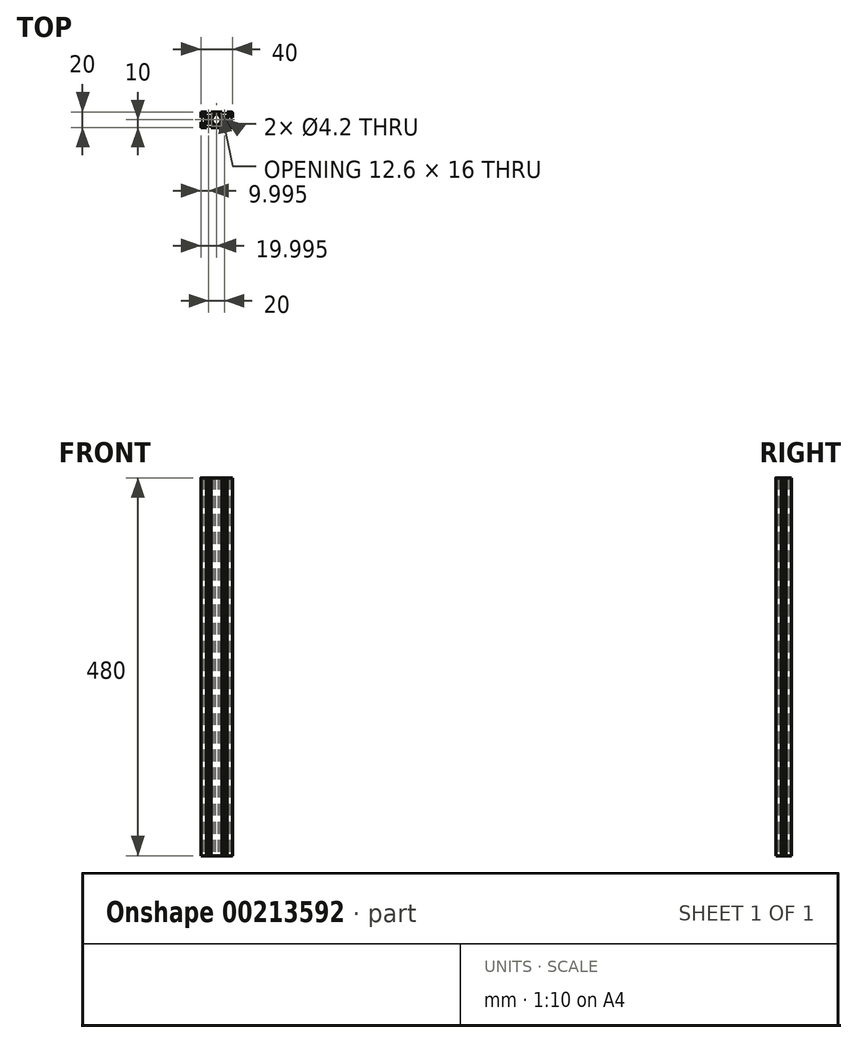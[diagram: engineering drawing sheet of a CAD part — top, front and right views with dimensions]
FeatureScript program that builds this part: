
annotation { "Feature Type Name" : "Feature", "Feature Type Description" : "" }
export const myFeature = defineFeature(function(context is Context, id is Id, definition is map)
    precondition{}
    {
        {
            var Q0;
            Q0=qCreatedBy(makeId("Top.planeOp"),FACE);
            var sketch = newSketch(context, id + "F0", { "sketchPlane" : qUnion([Q0])});
            skLineSegment(sketch, "E0.MirrorCS", {"start": v(6.14, -0.52) * mm, "end": v(6.44, 0) * mm});
            skLineSegment(sketch, "E1.MirrorCS", {"start": v(13.84, 0) * mm, "end": v(14.14, -0.52) * mm});
            skLineSegment(sketch, "E2.MirrorCS", {"start": v(10.65, -4) * mm, "end": v(10.14, -3.7) * mm});
            skLineSegment(sketch, "E3.MirrorCS", {"start": v(10.14, -3.7) * mm, "end": v(9.62, -4) * mm});
            skLineSegment(sketch, "E4.MirrorCS", {"start": v(4.14, -8) * mm, "end": v(7.14, -8) * mm});
            skLineSegment(sketch, "E5.MirrorCS", {"start": v(6.14, -2.94) * mm, "end": v(6.14, -0.52) * mm});
            skLineSegment(sketch, "E6.MirrorCS", {"start": v(16.14, -7.06) * mm, "end": v(13.07, -4) * mm});
            skLineSegment(sketch, "E7.MirrorCS", {"start": v(7.14, -8) * mm, "end": v(7.14, -10) * mm});
            skLineSegment(sketch, "E8.MirrorCS", {"start": v(20.14, -3) * mm, "end": v(20.14, -9) * mm});
            skLineSegment(sketch, "E9.MirrorCS", {"start": v(9.62, -4) * mm, "end": v(7.2, -4) * mm});
            skArc(sketch, "E10.MirrorCS", {"start": v(20.14, -9) * mm, "mid": v(19.84, -9.7) * mm, "end": v(19.14, -10) * mm});
            skLineSegment(sketch, "E11.MirrorCS", {"start": v(19.14, -10) * mm, "end": v(13.14, -10) * mm});
            skLineSegment(sketch, "E12.MirrorCS", {"start": v(13.07, -4) * mm, "end": v(10.65, -4) * mm});
            skLineSegment(sketch, "E13.MirrorCS", {"start": v(13.14, -10) * mm, "end": v(13.14, -8) * mm});
            skLineSegment(sketch, "E14.MirrorCS", {"start": v(14.14, -0.52) * mm, "end": v(14.14, -2.94) * mm});
            skLineSegment(sketch, "E15.MirrorCS", {"start": v(14.14, -2.94) * mm, "end": v(17.2, -6) * mm});
            skLineSegment(sketch, "E16.MirrorCS", {"start": v(17.2, -6) * mm, "end": v(18.14, -6) * mm});
            skLineSegment(sketch, "E17.MirrorCS", {"start": v(18.14, -6) * mm, "end": v(18.14, -3) * mm});
            skLineSegment(sketch, "E18.MirrorCS", {"start": v(18.14, -3) * mm, "end": v(20.14, -3) * mm});
            skLineSegment(sketch, "E19.MirrorCS", {"start": v(7.2, -4) * mm, "end": v(4.14, -7.06) * mm});
            skLineSegment(sketch, "E20.MirrorCS", {"start": v(13.14, -8) * mm, "end": v(16.14, -8) * mm});
            skLineSegment(sketch, "E21.MirrorCS", {"start": v(4.14, -7.06) * mm, "end": v(4.14, -8) * mm});
            skLineSegment(sketch, "E22.MirrorCS", {"start": v(16.14, -8) * mm, "end": v(16.14, -7.06) * mm});
            skLineSegment(sketch, "E23.MirrorCS", {"start": v(3.07, -6) * mm, "end": v(6.14, -2.94) * mm});
            skCircle(sketch, "E24", {"center": v(10.14, 0) * mm, "radius": 2.1 * mm});
            skLineSegment(sketch, "E25", {"start": v(3.07, -6) * mm, "end": v(2.01, -7.06) * mm});
            skLineSegment(sketch, "E26", {"start": v(2.01, -7.06) * mm, "end": v(2.01, -8) * mm});
            skLineSegment(sketch, "E27.MirrorCS", {"start": v(-10.38, -4) * mm, "end": v(-9.86, -3.7) * mm});
            skLineSegment(sketch, "E28.MirrorCS", {"start": v(-9.86, -3.7) * mm, "end": v(-9.35, -4) * mm});
            skLineSegment(sketch, "E29.MirrorCS", {"start": v(-13.56, 0) * mm, "end": v(-13.86, -0.52) * mm});
            skLineSegment(sketch, "E30.MirrorCS", {"start": v(-5.86, -0.52) * mm, "end": v(-6.16, 0) * mm});
            skLineSegment(sketch, "E31.MirrorCS", {"start": v(-12.86, -8) * mm, "end": v(-15.86, -8) * mm});
            skLineSegment(sketch, "E32.MirrorCS", {"start": v(-6.86, -8) * mm, "end": v(-6.86, -10) * mm});
            skLineSegment(sketch, "E33.MirrorCS", {"start": v(-19.86, -3) * mm, "end": v(-19.86, -9) * mm});
            skArc(sketch, "E34.MirrorCS", {"start": v(-19.86, -9) * mm, "mid": v(-19.57, -9.7) * mm, "end": v(-18.86, -10) * mm});
            skLineSegment(sketch, "E35.MirrorCS", {"start": v(-9.35, -4) * mm, "end": v(-6.93, -4) * mm});
            skLineSegment(sketch, "E36.MirrorCS", {"start": v(-18.86, -10) * mm, "end": v(-12.86, -10) * mm});
            skCircle(sketch, "E37.MirrorC", {"center": v(-9.86, 0) * mm, "radius": 2.1 * mm});
            skLineSegment(sketch, "E38.MirrorCS", {"start": v(-12.8, -4) * mm, "end": v(-10.38, -4) * mm});
            skLineSegment(sketch, "E39.MirrorCS", {"start": v(-17.86, -6) * mm, "end": v(-17.86, -3) * mm});
            skLineSegment(sketch, "E40.MirrorCS", {"start": v(-15.86, -8) * mm, "end": v(-15.86, -7.06) * mm});
            skLineSegment(sketch, "E41.MirrorCS", {"start": v(-13.86, -0.52) * mm, "end": v(-13.86, -2.94) * mm});
            skLineSegment(sketch, "E42.MirrorCS", {"start": v(-17.86, -3) * mm, "end": v(-19.86, -3) * mm});
            skLineSegment(sketch, "E43.MirrorCS", {"start": v(-13.86, -2.94) * mm, "end": v(-16.93, -6) * mm});
            skLineSegment(sketch, "E44.MirrorCS", {"start": v(-3.86, -8) * mm, "end": v(-6.86, -8) * mm});
            skLineSegment(sketch, "E45.MirrorCS", {"start": v(-15.86, -7.06) * mm, "end": v(-12.8, -4) * mm});
            skLineSegment(sketch, "E46.MirrorCS", {"start": v(-5.86, -2.94) * mm, "end": v(-5.86, -0.52) * mm});
            skLineSegment(sketch, "E47.MirrorCS", {"start": v(-6.93, -4) * mm, "end": v(-3.86, -7.06) * mm});
            skLineSegment(sketch, "E48.MirrorCS", {"start": v(-16.93, -6) * mm, "end": v(-17.86, -6) * mm});
            skLineSegment(sketch, "E49.MirrorCS", {"start": v(-1.74, -7.06) * mm, "end": v(-1.74, -8) * mm});
            skLineSegment(sketch, "E50.MirrorCS", {"start": v(-3.86, -7.06) * mm, "end": v(-3.86, -8) * mm});
            skLineSegment(sketch, "E51.MirrorCS", {"start": v(-2.8, -6) * mm, "end": v(-1.74, -7.06) * mm});
            skLineSegment(sketch, "E52.MirrorCS", {"start": v(-2.8, -6) * mm, "end": v(-5.86, -2.94) * mm});
            skLineSegment(sketch, "E53.MirrorCS", {"start": v(-12.86, -10) * mm, "end": v(-12.86, -8) * mm});
            skLineSegment(sketch, "E54.MirrorCS", {"start": v(10.14, 3.7) * mm, "end": v(9.62, 4) * mm});
            skLineSegment(sketch, "E55.MirrorCS", {"start": v(-10.38, 4) * mm, "end": v(-9.86, 3.7) * mm});
            skLineSegment(sketch, "E56.MirrorCS", {"start": v(10.65, 4) * mm, "end": v(10.14, 3.7) * mm});
            skLineSegment(sketch, "E57.MirrorCS", {"start": v(-9.86, 3.7) * mm, "end": v(-9.35, 4) * mm});
            skLineSegment(sketch, "E58.MirrorCS", {"start": v(13.84, 0) * mm, "end": v(14.14, 0.52) * mm});
            skLineSegment(sketch, "E59.MirrorCS", {"start": v(6.14, 0.52) * mm, "end": v(6.44, 0) * mm});
            skLineSegment(sketch, "E60.MirrorCS", {"start": v(-5.86, 0.52) * mm, "end": v(-6.16, 0) * mm});
            skLineSegment(sketch, "E61.MirrorCS", {"start": v(-13.56, 0) * mm, "end": v(-13.86, 0.52) * mm});
            skLineSegment(sketch, "E62.MirrorCS", {"start": v(-18.86, 10) * mm, "end": v(-12.86, 10) * mm});
            skLineSegment(sketch, "E63.MirrorCS", {"start": v(16.14, 7.06) * mm, "end": v(13.07, 4) * mm});
            skLineSegment(sketch, "E64.MirrorCS", {"start": v(6.14, 2.94) * mm, "end": v(6.14, 0.52) * mm});
            skLineSegment(sketch, "E65.MirrorCS", {"start": v(-3.86, 8) * mm, "end": v(-6.86, 8) * mm});
            skLineSegment(sketch, "E66.MirrorCS", {"start": v(4.14, 8) * mm, "end": v(7.14, 8) * mm});
            skLineSegment(sketch, "E67.MirrorCS", {"start": v(-15.86, 8) * mm, "end": v(-15.86, 7.06) * mm});
            skLineSegment(sketch, "E68.MirrorCS", {"start": v(-3.86, 7.06) * mm, "end": v(-3.86, 8) * mm});
            skArc(sketch, "E69.MirrorCS", {"start": v(20.14, 9) * mm, "mid": v(19.84, 9.7) * mm, "end": v(19.14, 10) * mm});
            skLineSegment(sketch, "E70.MirrorCS", {"start": v(14.14, 2.94) * mm, "end": v(17.2, 6) * mm});
            skLineSegment(sketch, "E71.MirrorCS", {"start": v(3.07, 6) * mm, "end": v(6.14, 2.94) * mm});
            skLineSegment(sketch, "E72.MirrorCS", {"start": v(-9.35, 4) * mm, "end": v(-6.93, 4) * mm});
            skLineSegment(sketch, "E73.MirrorCS", {"start": v(14.14, 0.52) * mm, "end": v(14.14, 2.94) * mm});
            skLineSegment(sketch, "E74.MirrorCS", {"start": v(-2.8, 6) * mm, "end": v(-5.86, 2.94) * mm});
            skLineSegment(sketch, "E75.MirrorCS", {"start": v(-17.86, 6) * mm, "end": v(-17.86, 3) * mm});
            skLineSegment(sketch, "E76.MirrorCS", {"start": v(16.14, 8) * mm, "end": v(16.14, 7.06) * mm});
            skLineSegment(sketch, "E77.MirrorCS", {"start": v(-15.86, 7.06) * mm, "end": v(-12.8, 4) * mm});
            skLineSegment(sketch, "E78.MirrorCS", {"start": v(18.14, 3) * mm, "end": v(20.14, 3) * mm});
            skLineSegment(sketch, "E79.MirrorCS", {"start": v(19.14, 10) * mm, "end": v(13.14, 10) * mm});
            skLineSegment(sketch, "E80.MirrorCS", {"start": v(4.14, 7.06) * mm, "end": v(4.14, 8) * mm});
            skLineSegment(sketch, "E81.MirrorCS", {"start": v(-12.86, 8) * mm, "end": v(-15.86, 8) * mm});
            skLineSegment(sketch, "E82.MirrorCS", {"start": v(-5.86, 2.94) * mm, "end": v(-5.86, 0.52) * mm});
            skLineSegment(sketch, "E83.MirrorCS", {"start": v(13.07, 4) * mm, "end": v(10.65, 4) * mm});
            skLineSegment(sketch, "E84.MirrorCS", {"start": v(-13.86, 2.94) * mm, "end": v(-16.93, 6) * mm});
            skLineSegment(sketch, "E85.MirrorCS", {"start": v(13.14, 8) * mm, "end": v(16.14, 8) * mm});
            skLineSegment(sketch, "E86.MirrorCS", {"start": v(-13.86, 0.52) * mm, "end": v(-13.86, 2.94) * mm});
            skLineSegment(sketch, "E87.MirrorCS", {"start": v(-6.86, 8) * mm, "end": v(-6.86, 10) * mm});
            skLineSegment(sketch, "E88.MirrorCS", {"start": v(20.14, 3) * mm, "end": v(20.14, 9) * mm});
            skLineSegment(sketch, "E89.MirrorCS", {"start": v(-12.8, 4) * mm, "end": v(-10.38, 4) * mm});
            skLineSegment(sketch, "E90.MirrorCS", {"start": v(-12.86, 10) * mm, "end": v(-12.86, 8) * mm});
            skLineSegment(sketch, "E91.MirrorCS", {"start": v(-6.93, 4) * mm, "end": v(-3.86, 7.06) * mm});
            skLineSegment(sketch, "E92.MirrorCS", {"start": v(9.62, 4) * mm, "end": v(7.2, 4) * mm});
            skLineSegment(sketch, "E93.MirrorCS", {"start": v(13.14, 10) * mm, "end": v(13.14, 8) * mm});
            skLineSegment(sketch, "E94.MirrorCS", {"start": v(-16.93, 6) * mm, "end": v(-17.86, 6) * mm});
            skLineSegment(sketch, "E95.MirrorCS", {"start": v(-19.86, 3) * mm, "end": v(-19.86, 9) * mm});
            skLineSegment(sketch, "E96.MirrorCS", {"start": v(3.07, 6) * mm, "end": v(2.01, 7.06) * mm});
            skLineSegment(sketch, "E97.MirrorCS", {"start": v(-17.86, 3) * mm, "end": v(-19.86, 3) * mm});
            skLineSegment(sketch, "E98.MirrorCS", {"start": v(-1.74, 7.06) * mm, "end": v(-1.74, 8) * mm});
            skLineSegment(sketch, "E99.MirrorCS", {"start": v(2.01, 7.06) * mm, "end": v(2.01, 8) * mm});
            skLineSegment(sketch, "E100.MirrorCS", {"start": v(18.14, 6) * mm, "end": v(18.14, 3) * mm});
            skArc(sketch, "E101.MirrorCS", {"start": v(-19.86, 9) * mm, "mid": v(-19.57, 9.7) * mm, "end": v(-18.86, 10) * mm});
            skLineSegment(sketch, "E102.MirrorCS", {"start": v(-2.8, 6) * mm, "end": v(-1.74, 7.06) * mm});
            skLineSegment(sketch, "E103.MirrorCS", {"start": v(7.14, 8) * mm, "end": v(7.14, 10) * mm});
            skLineSegment(sketch, "E104.MirrorCS", {"start": v(17.2, 6) * mm, "end": v(18.14, 6) * mm});
            skLineSegment(sketch, "E105.MirrorCS", {"start": v(7.2, 4) * mm, "end": v(4.14, 7.06) * mm});
            skLineSegment(sketch, "E106", {"start": v(7.14, -10) * mm, "end": v(-6.86, -10) * mm});
            skLineSegment(sketch, "E107", {"start": v(-1.74, -8) * mm, "end": v(2.01, -8) * mm});
            skLineSegment(sketch, "E108", {"start": v(-1.74, 8) * mm, "end": v(2.01, 8) * mm});
            skLineSegment(sketch, "E109", {"start": v(-6.86, 10) * mm, "end": v(7.14, 10) * mm});
            skLineSegment(sketch, "E110", {"start": v(-9.86, 0) * mm, "end": v(-19.86, 0) * mm, "construction": true});
            skSolve(sketch);
        }
        {
            var Q0;
            Q0=makeQuery(id+"F0.imprint","IMPRINT",FACE,{"disambiguationData":[TD([[makeQuery(id+"F0.imprint","IMPRINT",EDGE,{"derivedFrom":sQuery(id+"F0.wireOp",EDGE,"E0.MirrorCS")}),-1.0]])]});
            extrude(context, id + "F1", {"entities" : qUnion([Q0]), "depth" : 480 * mm});
        }
    });
